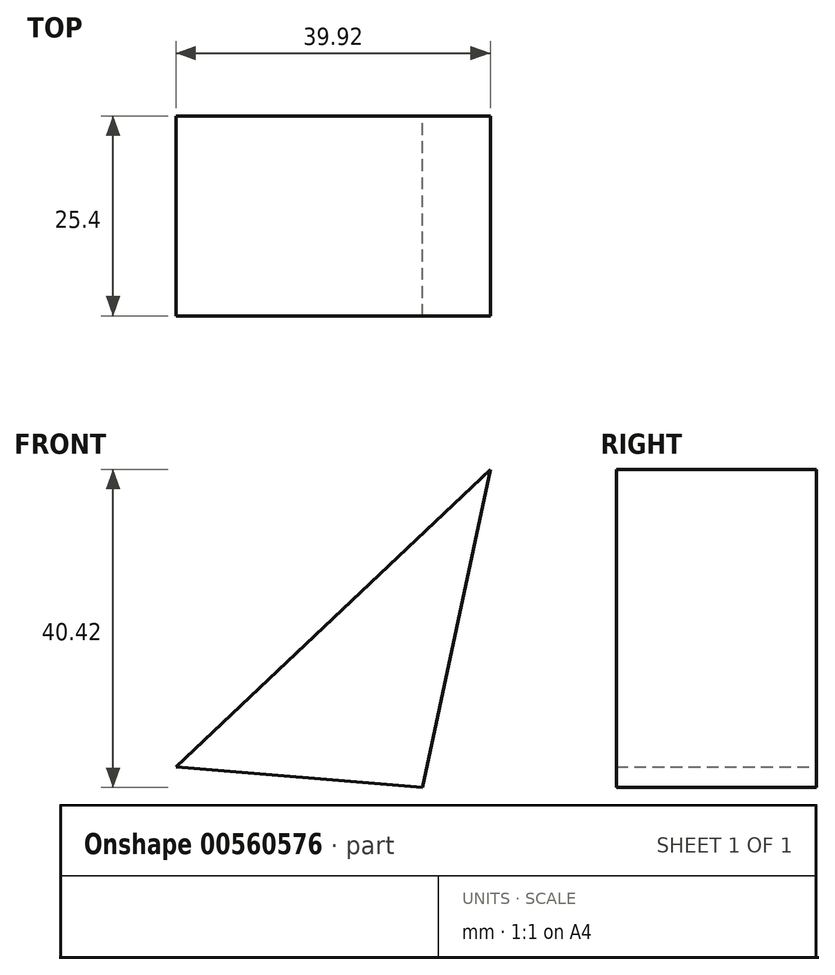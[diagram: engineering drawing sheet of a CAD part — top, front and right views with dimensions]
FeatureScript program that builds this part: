
annotation { "Feature Type Name" : "Feature", "Feature Type Description" : "" }
export const myFeature = defineFeature(function(context is Context, id is Id, definition is map)
    precondition{}
    {
        {
            var Q0;
            Q0=qCreatedBy(makeId("Front.planeOp"),FACE);
            var sketch = newSketch(context, id + "F0", { "sketchPlane" : qUnion([Q0])});
            skLineSegment(sketch, "E0", {"start": v(0, 0) * mm, "end": v(31.34, -2.63) * mm});
            skLineSegment(sketch, "E1", {"start": v(31.34, -2.63) * mm, "end": v(39.92, 37.8) * mm});
            skLineSegment(sketch, "E2", {"start": v(39.92, 37.8) * mm, "end": v(0, 0) * mm});
            skSolve(sketch);
        }
        {
            var Q0;
            Q0=makeQuery(id+"F0.imprint","IMPRINT",FACE,{"disambiguationData":[TD([[makeQuery(id+"F0.imprint","IMPRINT",EDGE,{"derivedFrom":sQuery(id+"F0.wireOp",EDGE,"E0")}),1.0]])]});
            extrude(context, id + "F1", {"entities" : qUnion([Q0]), "depth" : 25.4 * mm, "offsetDistance" : 25.4 * mm});
        }
    });
